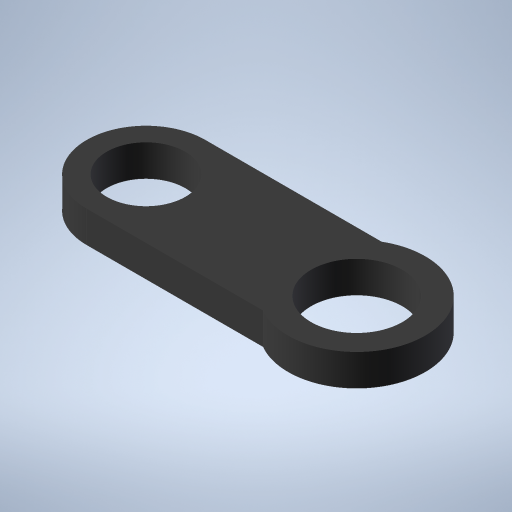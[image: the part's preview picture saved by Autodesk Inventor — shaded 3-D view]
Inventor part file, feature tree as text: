
AUTODESK INVENTOR PART (.ipt)
format: ipt  version: 2023 (Build 270158000, 158)  size: 239,616 bytes
history: native  units: in
note: dims shown in document units (in); Inventor stores cm internally (conversion verified against a paired STEP export)
features: extrude x1, sketch x1
ambient origin geometry x8: Origin, YZ Plane, XZ Plane, XY Plane, X Axis, Y Axis, Z Axis, Center Point
bodies: Solid1 (feature_tree)
feature tree (2):
  extrude  "Extrusion1"  Depth=1.125in
  sketch  "Sketch1"  dims[d5=0.3in d6=0.0in d11=0.747in d14=1.125in d3=0.5in d4=0.0344in]
